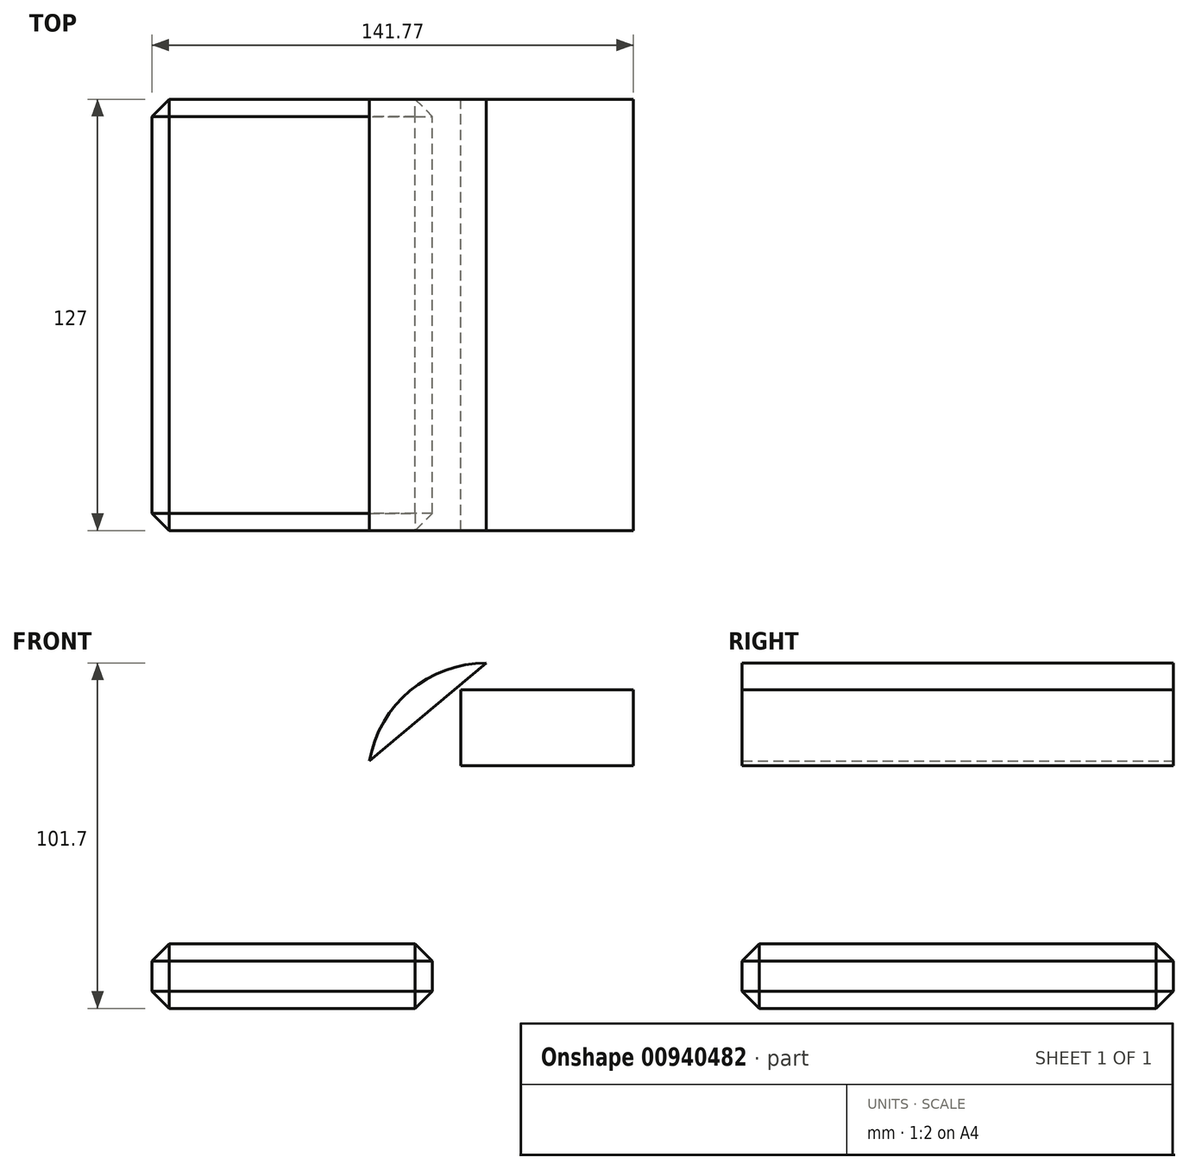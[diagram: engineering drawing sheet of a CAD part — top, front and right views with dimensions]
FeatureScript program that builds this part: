
annotation { "Feature Type Name" : "Feature", "Feature Type Description" : "" }
export const myFeature = defineFeature(function(context is Context, id is Id, definition is map)
    precondition{}
    {
        {
            var Q0;
            Q0=qCreatedBy(makeId("Front.planeOp"),FACE);
            var sketch = newSketch(context, id + "F0", { "sketchPlane" : qUnion([Q0])});
            skLineSegment(sketch, "E0.bottom", {"start": v(41.27, 9.53) * mm, "end": v(-41.28, 9.53) * mm});
            skLineSegment(sketch, "E0.top", {"start": v(41.28, -9.52) * mm, "end": v(-41.27, -9.52) * mm});
            skLineSegment(sketch, "E0.left", {"start": v(41.28, 9.53) * mm, "end": v(41.28, -9.52) * mm});
            skLineSegment(sketch, "E0.right", {"start": v(-41.28, 9.53) * mm, "end": v(-41.27, -9.52) * mm});
            skPoint(sketch, "E0.middle", {"position": v(0, 0) * mm});
            skLineSegment(sketch, "E1.bottom", {"start": v(100.5, 61.95) * mm, "end": v(49.7, 61.95) * mm});
            skLineSegment(sketch, "E1.top", {"start": v(100.5, 84.28) * mm, "end": v(49.7, 84.28) * mm});
            skLineSegment(sketch, "E1.left", {"start": v(100.5, 61.95) * mm, "end": v(100.5, 84.28) * mm});
            skLineSegment(sketch, "E1.right", {"start": v(49.7, 61.95) * mm, "end": v(49.7, 84.28) * mm});
            skPoint(sketch, "E1.middle", {"position": v(75.1, 73.12) * mm});
            skLineSegment(sketch, "E2", {"start": v(41.27, 9.53) * mm, "end": v(41.27, 57.24) * mm});
            skArc(sketch, "E3", {"start": v(41.27, 57.24) * mm, "mid": v(45.92, 68.47) * mm, "end": v(57.15, 73.12) * mm});
            skLineSegment(sketch, "E4", {"start": v(57.15, 73.12) * mm, "end": v(75.1, 73.12) * mm});
            skArc(sketch, "E5.0", {"start": v(22.22, 57.24) * mm, "mid": v(32.45, 81.94) * mm, "end": v(57.15, 92.17) * mm});
            skFitSpline(sketch, "E6", {"points": [v(-41.28, 9.53) * mm, v(57.15, 92.17) * mm], "startDerivative": vector(98.42, 82.64) * mm, "endDerivative": vector(98.42, 82.64) * mm});
            skSolve(sketch);
        }
        {
            var Q0;
            Q0 = qSketchRegion(id + "F0", true);
            var Q1;
            Q1=makeQuery(id+"F0.imprint","IMPRINT",FACE,{"disambiguationData":[TD([[makeQuery(id+"F0.imprint","IMPRINT",EDGE,{"derivedFrom":sQuery(id+"F0.wireOp",EDGE,"E0.bottom")}),1.0]])]});
            extrude(context, id + "F1", {"entities" : qUnion([Q0, Q1]), "endBound" : BoundingType.SYMMETRIC, "depth" : 127 * mm, "offsetDistance" : 25.4 * mm});
        }
        {
            var Q0;
            Q0=makeQuery(id+"F1.opExtrude","SWEPT_FACE",FACE,{"disambiguationData":[OSD([sQuery(id+"F0.wireOp",EDGE,"E0.left")])]});
            var Q1;
            Q1=makeQuery(id+"F1.opExtrude","CAP_FACE",FACE,{"disambiguationData":[OSD([sQuery(id+"F0.wireOp",EDGE,"E0.bottom"),sQuery(id+"F0.wireOp",EDGE,"E0.top"),sQuery(id+"F0.wireOp",EDGE,"E0.left"),sQuery(id+"F0.wireOp",EDGE,"E0.right")])],"isStart":false});
            var Q2;
            Q2=makeQuery(id+"F1.opExtrude","CAP_FACE",FACE,{"disambiguationData":[OSD([sQuery(id+"F0.wireOp",EDGE,"E0.bottom"),sQuery(id+"F0.wireOp",EDGE,"E0.top"),sQuery(id+"F0.wireOp",EDGE,"E0.left"),sQuery(id+"F0.wireOp",EDGE,"E0.right")])],"isStart":true});
            var Q3;
            Q3=makeQuery(id+"F1.opExtrude","SWEPT_FACE",FACE,{"disambiguationData":[OSD([sQuery(id+"F0.wireOp",EDGE,"E0.right")])]});
            chamfer(context, id + "F2", {"entities" : qUnion([Q0, Q1, Q2, Q3]), "width" : 5.08 * mm, "tangentPropagation" : true});
        }
    });
